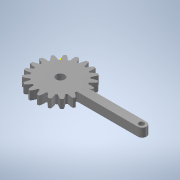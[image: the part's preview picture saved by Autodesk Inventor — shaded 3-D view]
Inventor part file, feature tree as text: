
AUTODESK INVENTOR PART (.ipt)
format: ipt  version: 2022 (Build 260153000, 153)  size: 325,632 bytes
history: native  units: mm (DEFAULTED — no unit token found)
features: sketch x8, extrude x6, plane x3, other x3, fillet x1
ambient origin geometry x8: Origin, YZ Plane, XZ Plane, XY Plane, X Axis, Y Axis, Z Axis, Center Point
bodies: Solid1 (feature_tree)
feature tree (21):
  extrude  "Extrusion1"  Depth=14.0mm TaperAngle=0.0deg
  plane  "Work Plane2"
  plane  "Work Plane8"
  plane  "Work Plane9"
  other  "Spur Gear"
  extrude  "Extrusion2"  Depth=10.0mm TaperAngle=0.0deg
  sketch  "Sketch4"  dims[d39=0.0mm d41=0.0mm]
  extrude  "Extrusion3"  Depth=1.65347mm TaperAngle=0.0deg
  extrude  "Extrusion4"  TaperAngle=0.0deg  [1 undecoded]
  extrude  "Extrusion8"  Depth=63.0mm
  extrude  "Extrusion9"  Depth=8.0mm
  fillet  "Fillet2"  Radius=3.0mm
  sketch  "Sketch1"  dims[d0=31.5mm d1=14.0mm d2=0.0mm]
  sketch  "Sketch2"  dims[d3=28.5mm d4=10.0mm d5=0.0mm]
  other  "Srf1"
  sketch  "Sketch3"  dims[d16=63.0mm d17=0.0mm d34=1.65347mm]
  sketch  "Sketch5"  dims[d43=63.0mm d46=63.0mm]
  sketch  "Sketch6"  dims[d47=0.0mm d48=0.0mm d49=8.0mm d50=3.0mm]
  sketch  "Sketch11"  dims[d51=1.4mm]
  sketch  "Sketch12"  dims[d52=10.0mm d53=0.0mm d54=14.0mm d55=0.0mm d57=47.0mm d58=0.0mm d72=50.0mm d73=2.5mm d74=2.5mm d75=5.0mm d76=0.0mm d77=5.0mm d81=3.0mm d82=5.0mm d83=0.0mm d84=2.5mm d78=0.872665mm]
  other  "Pitch Diameter"
note: 1 required parameter value undecoded (feature->parameter linkage not recoverable at this tier; creation-order binding heuristic only, values carry confidence <= 0.55)
